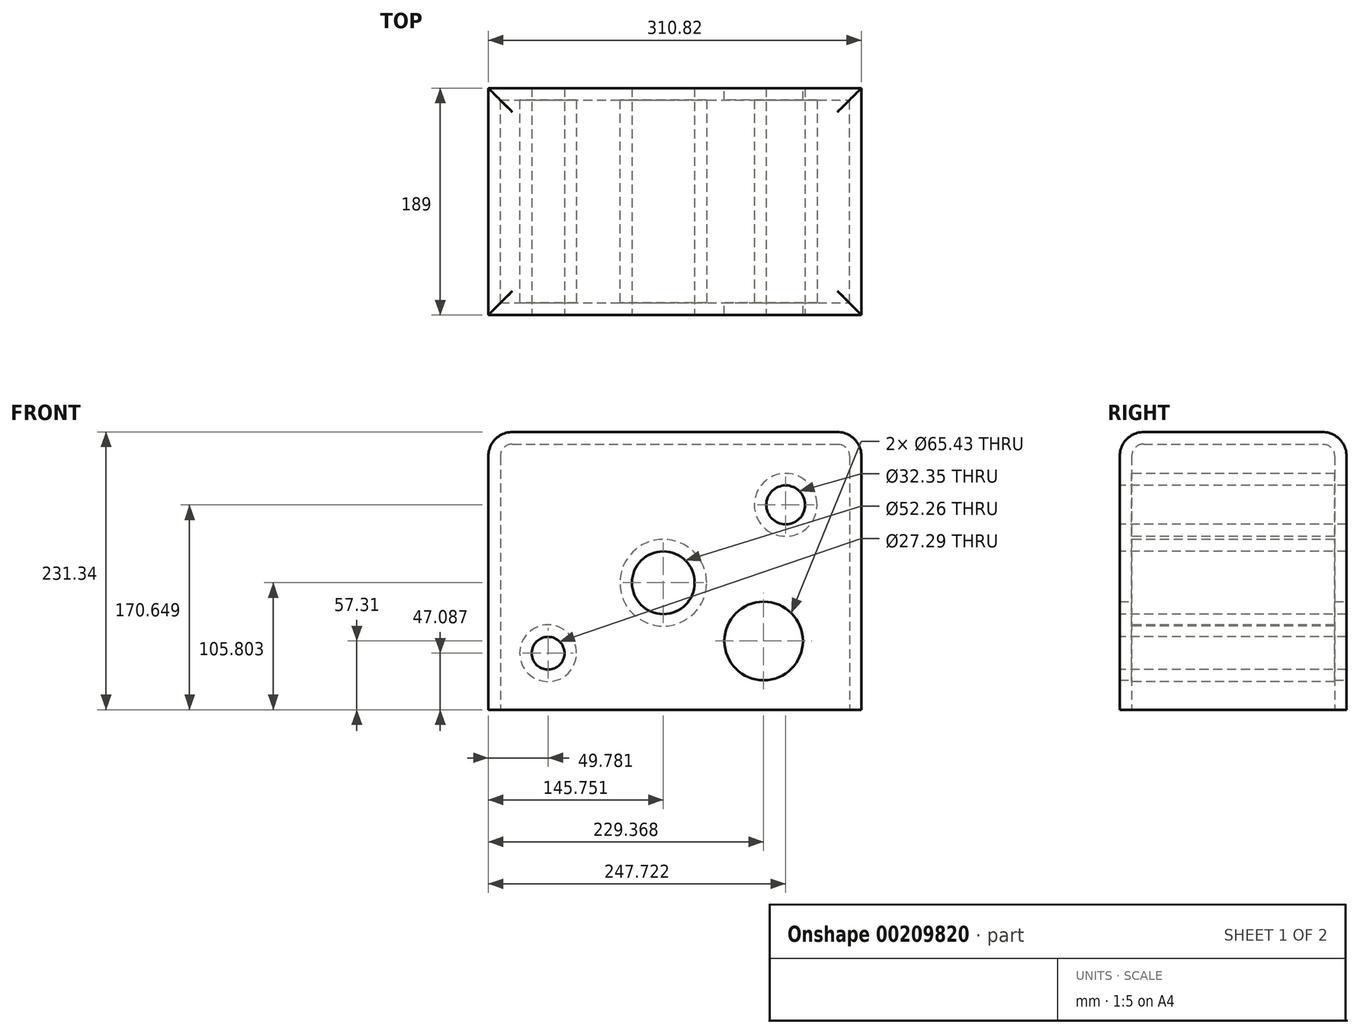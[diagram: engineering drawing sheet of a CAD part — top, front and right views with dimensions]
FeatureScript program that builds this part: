
annotation { "Feature Type Name" : "Feature", "Feature Type Description" : "" }
export const myFeature = defineFeature(function(context is Context, id is Id, definition is map)
    precondition{}
    {
        {
            var Q0;
            Q0=qCreatedBy(makeId("Front.planeOp"),FACE);
            var sketch = newSketch(context, id + "F0", { "sketchPlane" : qUnion([Q0])});
            skLineSegment(sketch, "E0.bottom", {"start": v(-155.41, 115.67) * mm, "end": v(155.41, 115.67) * mm});
            skLineSegment(sketch, "E0.top", {"start": v(-155.41, -115.67) * mm, "end": v(155.41, -115.67) * mm});
            skLineSegment(sketch, "E0.left", {"start": v(-155.41, 115.67) * mm, "end": v(-155.41, -115.67) * mm});
            skLineSegment(sketch, "E0.right", {"start": v(155.41, 115.67) * mm, "end": v(155.41, -115.67) * mm});
            skPoint(sketch, "E0.middle", {"position": v(0, 0) * mm});
            skSolve(sketch);
        }
        {
            var Q0;
            Q0=makeQuery(id+"F0.imprint","IMPRINT",FACE,{"disambiguationData":[TD([[makeQuery(id+"F0.imprint","IMPRINT",EDGE,{"derivedFrom":sQuery(id+"F0.wireOp",EDGE,"E0.bottom")}),-1.0]])]});
            extrude(context, id + "F1", {"entities" : qUnion([Q0]), "depth" : 189 * mm});
        }
        {
            var Q0;
            Q0=makeQuery(id+"F1.opExtrude","SWEPT_FACE",FACE,{"disambiguationData":[OSD([sQuery(id+"F0.wireOp",EDGE,"E0.bottom")])]});
            fillet(context, id + "F2", {"entities" : qUnion([Q0]), "radius" : 20 * mm, "tangentPropagation" : true, "allowEdgeOverflow" : false});
        }
        {
            var Q0;
            Q0=makeQuery(id+"F1.opExtrude","CAP_FACE",FACE,{"disambiguationData":[OSD([sQuery(id+"F0.wireOp",EDGE,"E0.bottom"),sQuery(id+"F0.wireOp",EDGE,"E0.top"),sQuery(id+"F0.wireOp",EDGE,"E0.left"),sQuery(id+"F0.wireOp",EDGE,"E0.right")])],"isStart":false});
            var sketch = newSketch(context, id + "F3", { "sketchPlane" : qUnion([Q0])});
            skCircle(sketch, "E1", {"center": v(-105.63, -68.58) * mm, "radius": 13.64 * mm});
            skCircle(sketch, "E2", {"center": v(-9.66, -9.87) * mm, "radius": 26.13 * mm});
            skCircle(sketch, "E3", {"center": v(92.31, 54.98) * mm, "radius": 16.17 * mm});
            skSolve(sketch);
        }
        {
            var Q0;
            Q0 = qSketchRegion(id + "F3", true);
            extrude(context, id + "F4", {"entities" : qUnion([Q0]), "operationType" : NewBodyOperationType.REMOVE, "endBound" : BoundingType.THROUGH_ALL, "oppositeDirection" : true, "depth" : 25 * mm});
        }
        {
            var Q0;
            Q0=makeQuery(id+"F1.opExtrude","SWEPT_FACE",FACE,{"disambiguationData":[OSD([sQuery(id+"F0.wireOp",EDGE,"E0.top")])]});
            shell(context, id + "F5", {"entities" : qUnion([Q0]), "thickness" : 10 * mm});
        }
        {
            var Q0;
            Q0=makeQuery(id+"F1.opExtrude","CAP_FACE",FACE,{"disambiguationData":[OSD([sQuery(id+"F0.wireOp",EDGE,"E0.bottom"),sQuery(id+"F0.wireOp",EDGE,"E0.top"),sQuery(id+"F0.wireOp",EDGE,"E0.left"),sQuery(id+"F0.wireOp",EDGE,"E0.right")])],"isStart":true});
            var sketch = newSketch(context, id + "F6", { "sketchPlane" : qUnion([Q0])});
            skCircle(sketch, "E4", {"center": v(-73.96, -58.36) * mm, "radius": 32.72 * mm});
            skSolve(sketch);
        }
        {
            var Q0;
            Q0 = qSketchRegion(id + "F6", true);
            extrude(context, id + "F7", {"entities" : qUnion([Q0]), "operationType" : NewBodyOperationType.REMOVE, "endBound" : BoundingType.THROUGH_ALL, "oppositeDirection" : true, "depth" : 25 * mm});
        }
    });
